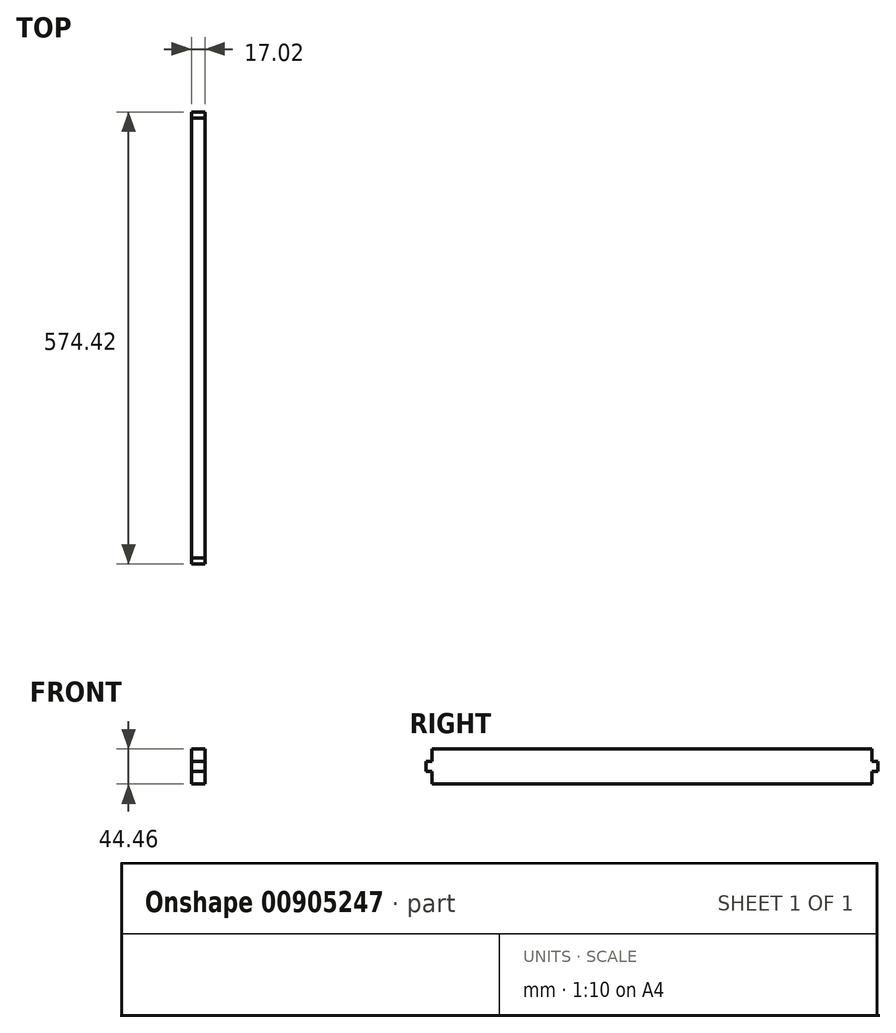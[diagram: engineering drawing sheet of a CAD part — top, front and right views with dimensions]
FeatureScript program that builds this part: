
annotation { "Feature Type Name" : "Feature", "Feature Type Description" : "" }
export const myFeature = defineFeature(function(context is Context, id is Id, definition is map)
    precondition{}
    {
        {
            var Q0;
            Q0=qCreatedBy(makeId("Right.planeOp"),FACE);
            var sketch = newSketch(context, id + "F0", { "sketchPlane" : qUnion([Q0])});
            skLineSegment(sketch, "E0.bottom", {"start": v(287.21, -22.23) * mm, "end": v(-287.21, -22.23) * mm});
            skLineSegment(sketch, "E0.top", {"start": v(287.21, 22.23) * mm, "end": v(-287.21, 22.22) * mm});
            skLineSegment(sketch, "E0.left", {"start": v(287.21, -22.23) * mm, "end": v(287.21, 22.22) * mm});
            skLineSegment(sketch, "E0.right", {"start": v(-287.21, -22.23) * mm, "end": v(-287.21, 22.22) * mm});
            skPoint(sketch, "E0.middle", {"position": v(0, 0) * mm});
            skSolve(sketch);
        }
        {
            var Q0;
            Q0=qSketchRegion(id+"F0",true);
            extrude(context, id + "F1", {"entities" : qUnion([Q0]), "offsetDistance" : 25.4 * mm, "depth" : 17.02 * mm});
        }
        {
            var Q0;
            Q0=makeQuery(id+"F1.opExtrude","CAP_FACE",FACE,{"disambiguationData":[OSD([sQuery(id+"F0.wireOp",EDGE,"E0.bottom"),sQuery(id+"F0.wireOp",EDGE,"E0.top"),sQuery(id+"F0.wireOp",EDGE,"E0.left"),sQuery(id+"F0.wireOp",EDGE,"E0.right")])],"isStart":false});
            var sketch = newSketch(context, id + "F2", { "sketchPlane" : qUnion([Q0])});
            skLineSegment(sketch, "E1.bottom", {"start": v(-287.21, 22.22) * mm, "end": v(-279.27, 22.22) * mm});
            skLineSegment(sketch, "E1.top", {"start": v(-287.21, 6.35) * mm, "end": v(-279.27, 6.35) * mm});
            skLineSegment(sketch, "E1.left", {"start": v(-287.21, 22.22) * mm, "end": v(-287.21, 6.35) * mm});
            skLineSegment(sketch, "E1.right", {"start": v(-279.27, 22.22) * mm, "end": v(-279.27, 6.35) * mm});
            skLineSegment(sketch, "E2.bottom", {"start": v(-287.21, -22.23) * mm, "end": v(-279.27, -22.23) * mm});
            skLineSegment(sketch, "E2.top", {"start": v(-287.21, -6.35) * mm, "end": v(-279.27, -6.35) * mm});
            skLineSegment(sketch, "E2.left", {"start": v(-287.21, -22.23) * mm, "end": v(-287.21, -6.35) * mm});
            skLineSegment(sketch, "E2.right", {"start": v(-279.27, -22.23) * mm, "end": v(-279.27, -6.35) * mm});
            skLineSegment(sketch, "E3.MirrorCS", {"start": v(287.21, 22.22) * mm, "end": v(279.27, 22.22) * mm});
            skLineSegment(sketch, "E4.MirrorCS", {"start": v(287.21, 6.35) * mm, "end": v(279.27, 6.35) * mm});
            skLineSegment(sketch, "E5.MirrorCS", {"start": v(279.27, -22.23) * mm, "end": v(279.27, -6.35) * mm});
            skLineSegment(sketch, "E6.MirrorCS", {"start": v(287.21, 22.22) * mm, "end": v(287.21, 6.35) * mm});
            skLineSegment(sketch, "E7.MirrorCS", {"start": v(279.27, 22.22) * mm, "end": v(279.27, 6.35) * mm});
            skLineSegment(sketch, "E8.MirrorCS", {"start": v(287.21, -22.23) * mm, "end": v(279.27, -22.23) * mm});
            skLineSegment(sketch, "E9.MirrorCS", {"start": v(287.21, -22.23) * mm, "end": v(287.21, -6.35) * mm});
            skLineSegment(sketch, "E10.MirrorCS", {"start": v(287.21, -6.35) * mm, "end": v(279.27, -6.35) * mm});
            skSolve(sketch);
        }
        {
            var Q0;
            Q0=qSketchRegion(id+"F2",true);
            extrude(context, id + "F3", {"entities" : qUnion([Q0]), "operationType" : NewBodyOperationType.REMOVE, "oppositeDirection" : true, "depth" : 25.4 * mm});
        }
    });
